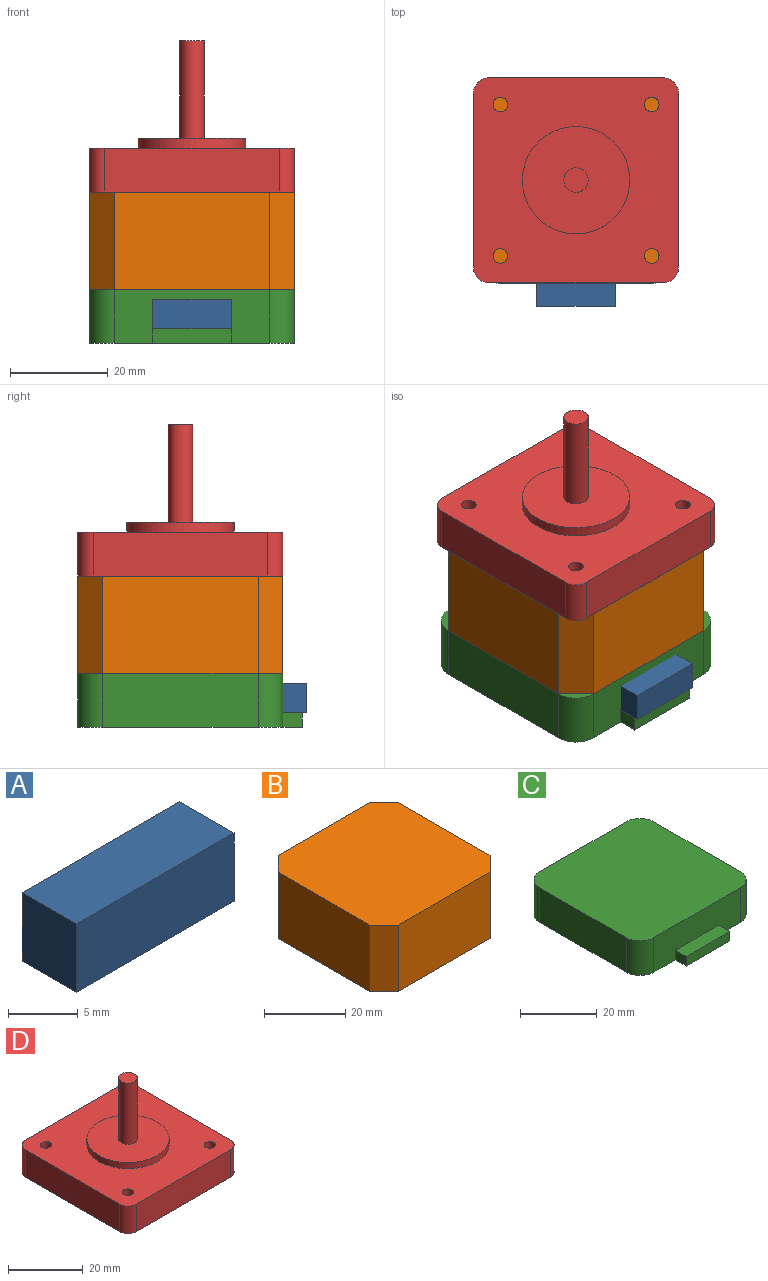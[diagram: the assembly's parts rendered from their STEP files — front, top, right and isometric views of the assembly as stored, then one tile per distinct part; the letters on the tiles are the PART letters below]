
ASSEMBLY  parts=4 mates=3
PART A: 6 faces, bbox 16x5.5x6 mm
  f0: plane 16x5.5mm, normal (0,0,-1), area 88mm2, adj f1,f3,f4,f5
  f1: plane 6x5.5mm, normal (1,0,0), area 33mm2, adj f0,f2,f4,f5
  f2: plane 16x5.5mm, normal (0,0,1), area 88mm2, adj f1,f3,f4,f5
  f3: plane 6x5.5mm, normal (-1,0,0), area 33mm2, adj f0,f2,f4,f5
  f4: plane 16x6mm, normal (0,-1,0), area 96mm2, adj f0,f1,f2,f3
  f5: plane 16x6mm, normal (0,1,0), area 96mm2, adj f0,f1,f2,f3
PART B: 10 faces, bbox 42x42x20 mm
  f0: plane 31.84x20mm, normal (1,0,0), area 636.8mm2, adj f1,f7,f8,f9
  f1: plane 20x5.08mm, normal (0.71,-0.71,0), area 143.7mm2, adj f0,f2,f8,f9
  f2: plane 31.84x20mm, normal (0,-1,0), area 636.8mm2, adj f1,f3,f8,f9
  f3: plane 20x5.08mm, normal (-0.71,-0.71,0), area 143.7mm2, adj f2,f4,f8,f9
  f4: plane 31.84x20mm, normal (-1,0,0), area 636.8mm2, adj f3,f5,f8,f9
  f5: plane 20x5.08mm, normal (-0.71,0.71,0), area 143.7mm2, adj f4,f6,f8,f9
  f6: plane 31.84x20mm, normal (0,1,0), area 636.8mm2, adj f5,f7,f8,f9
  f7: plane 20x5.08mm, normal (0.71,0.71,0), area 143.7mm2, adj f0,f6,f8,f9
  f8: plane 42x42mm, normal (0,0,-1), area 1712.4mm2, adj f0,f1,f2,f3,f4,f5,f6,f7
  f9: plane 42x42mm, normal (0,0,1), area 1712.4mm2, adj f0,f1,f2,f3,f4,f5,f6,f7
PART C: 14 faces, bbox 42x46x11 mm
  f0: plane 31.84x11mm, normal (0,-1,0), area 302.2mm2, adj f4,f5,f6,f7,f10,f11,f12
  f1: plane 31.84x11mm, normal (-1,0,0), area 350.2mm2, adj f4,f5,f6,f8
  f2: plane 31.84x11mm, normal (0,1,0), area 350.2mm2, adj f4,f5,f8,f9
  f3: plane 31.84x11mm, normal (1,0,0), area 350.2mm2, adj f4,f5,f7,f9
  f4: plane 46x42mm, normal (0,0,-1), area 1805.8mm2, adj f0,f1,f2,f3,f6,f7,f8,f9
  f5: plane 42x42mm, normal (0,0,1), area 1741.8mm2, adj f0,f1,f2,f3,f6,f7,f8,f9
  f6: cylinder r=5.08mm len=11mm, axis (0,0,-1), area 87.8mm2, adj f0,f1,f4,f5
  f7: cylinder r=5.08mm len=11mm, axis (0,0,1), area 87.8mm2, adj f0,f3,f4,f5
  f8: cylinder r=5.08mm len=11mm, axis (0,0,1), area 87.8mm2, adj f1,f2,f4,f5
  f9: cylinder r=5.08mm len=11mm, axis (0,0,-1), area 87.8mm2, adj f2,f3,f4,f5
  f10: plane 4x3mm, normal (-1,0,0), area 12mm2, adj f0,f4,f12,f13
  f11: plane 4x3mm, normal (1,0,0), area 12mm2, adj f0,f4,f12,f13
  f12: plane 16x4mm, normal (0,0,1), area 64mm2, adj f0,f10,f11,f13
  f13: plane 16x3mm, normal (0,-1,0), area 48mm2, adj f4,f10,f11,f12
PART D: 18 faces, bbox 42x42x31 mm
  f0: plane 35.65x9mm, normal (-1,0,0), area 320.8mm2, adj f4,f5,f8,f11
  f1: plane 35.65x9mm, normal (0,-1,0), area 320.8mm2, adj f4,f5,f8,f9
  f2: plane 35.65x9mm, normal (1,0,0), area 320.8mm2, adj f4,f5,f9,f10
  f3: plane 35.65x9mm, normal (0,1,0), area 320.8mm2, adj f4,f5,f10,f11
  f4: plane 42x42mm, normal (0,0,1), area 1346.9mm2, adj f0,f1,f2,f3,f6,f8,f9,f10
  f5: plane 42x42mm, normal (0,0,-1), area 1727.1mm2, adj f0,f1,f2,f3,f8,f9,f10,f11
  f6: cylinder r=11mm len=22mm, axis (0,0,-1), area 138.2mm2, adj f4,f7
  f7: plane 22x22mm, normal (0,0,1), area 360.5mm2, adj f6,f16
  f8: cylinder r=3.17mm len=9mm, axis (0,0,-1), area 44.9mm2, adj f0,f1,f4,f5
  f9: cylinder r=3.17mm len=9mm, axis (0,0,1), area 44.9mm2, adj f1,f2,f4,f5
  f10: cylinder r=3.17mm len=9mm, axis (0,0,-1), area 44.9mm2, adj f2,f3,f4,f5
  f11: cylinder r=3.17mm len=9mm, axis (0,0,1), area 44.9mm2, adj f0,f3,f4,f5
  f12: cylinder r=1.5mm len=9mm, axis (0,0,1), area 84.8mm2, adj f4,f5
  f13: cylinder r=1.5mm len=9mm, axis (0,0,1), area 84.8mm2, adj f4,f5
  f14: cylinder r=1.5mm len=9mm, axis (0,0,1), area 84.8mm2, adj f4,f5
  f15: cylinder r=1.5mm len=9mm, axis (0,0,1), area 84.8mm2, adj f4,f5
  f16: cylinder r=2.5mm len=20mm, axis (0,0,-1), area 314.2mm2, adj f7,f17
  f17: plane 5x5mm, normal (0,0,1), area 19.6mm2, adj f16
PLACE A t=(0,0.75,2.4)mm
PLACE B t=(0,0,2.4)mm
PLACE C t=(0,0,2.4)mm
PLACE D t=(0,0,2.4)mm
MATE fastened A.f0 <-> C.f12  axis (0,0,-1) through (0.96,-27.32,-25.6)mm
MATE fastened D.f6 <-> B.f9  axis (0,0,-1) through (0.96,-4.32,2.4)mm
MATE fastened C.f5 <-> B.f8  axis (0,0,1) through (0.96,-4.32,-17.6)mm
